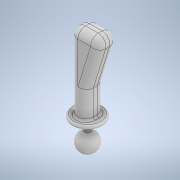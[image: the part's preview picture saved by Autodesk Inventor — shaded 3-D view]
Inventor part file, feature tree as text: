
AUTODESK INVENTOR PART (.ipt)
format: ipt  version: 2021 (Build 250183000, 183)  size: 187,904 bytes
history: native  units: mm
features: fillet x3, sketch x2, extrude x1, plane x1, revolve x1
ambient origin geometry x8: Origin, YZ Plane, XZ Plane, XY Plane, X Axis, Y Axis, Z Axis, Center Point
bodies: Solid1 (feature_tree)
feature tree (8):
  extrude  "Extrusion1"  Depth=20.0mm
  plane  "Work Plane1"
  revolve  "Revolution1"  [1 undecoded]
  fillet  "Fillet5"  Radius=20.0mm
  fillet  "Fillet6"  Radius=25.0mm
  fillet  "Fillet7"  [1 undecoded]
  sketch  "Sketch1"  dims[d0=100.0mm d1=20.0mm]
  sketch  "Sketch2"  dims[d4=25.0mm d5=0.0mm d6=5.0mm d7=20.0mm d10=25.0mm d11=90.0deg d16=20.0mm d17=65.0mm d18=10.0mm d19=10.0mm d20=2.5mm d21=3.75mm]
note: 2 required parameter values undecoded (feature->parameter linkage not recoverable at this tier; creation-order binding heuristic only, values carry confidence <= 0.55)